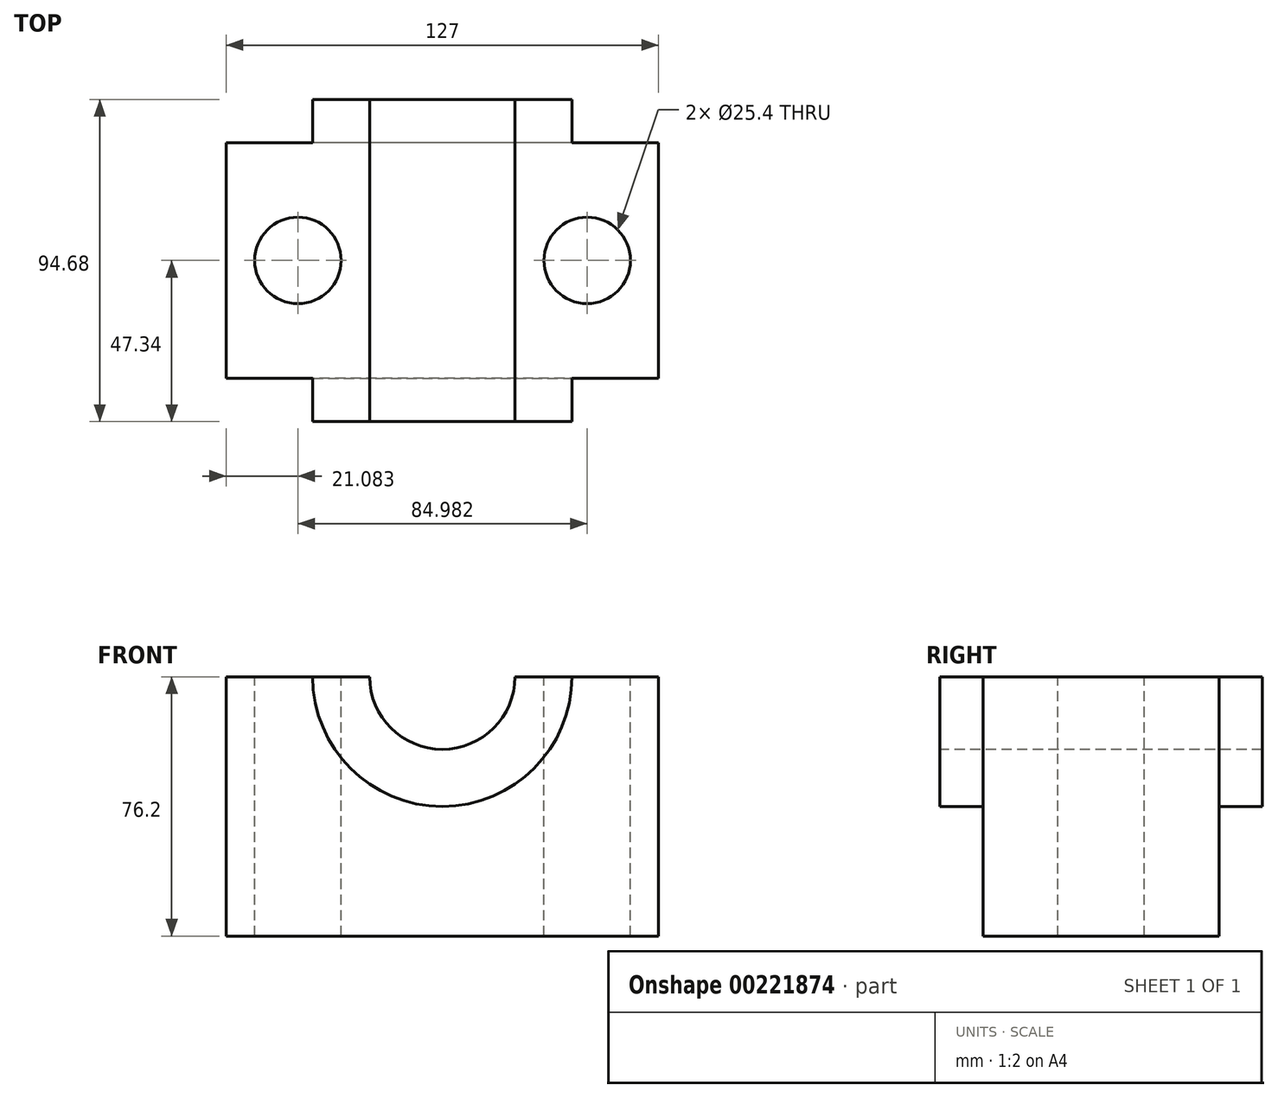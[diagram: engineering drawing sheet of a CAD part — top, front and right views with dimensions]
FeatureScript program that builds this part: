
annotation { "Feature Type Name" : "Feature", "Feature Type Description" : "" }
export const myFeature = defineFeature(function(context is Context, id is Id, definition is map)
    precondition{}
    {
        {
            var Q0;
            Q0=qCreatedBy(makeId("Top.planeOp"),FACE);
            var sketch = newSketch(context, id + "F0", { "sketchPlane" : qUnion([Q0])});
            skLineSegment(sketch, "E0.bottom", {"start": v(63.5, -34.64) * mm, "end": v(38.1, -34.64) * mm});
            skLineSegment(sketch, "E0.top", {"start": v(63.5, 34.64) * mm, "end": v(38.1, 34.64) * mm});
            skLineSegment(sketch, "E0.left", {"start": v(63.5, -34.64) * mm, "end": v(63.5, 34.64) * mm});
            skLineSegment(sketch, "E0.right", {"start": v(-63.5, -34.64) * mm, "end": v(-63.5, 34.64) * mm});
            skPoint(sketch, "E0.middle", {"position": v(0, 0) * mm});
            skLineSegment(sketch, "E1.bottom", {"start": v(-38.1, 47.34) * mm, "end": v(38.1, 47.34) * mm});
            skLineSegment(sketch, "E1.top", {"start": v(-38.1, -47.34) * mm, "end": v(38.1, -47.34) * mm});
            skLineSegment(sketch, "E1.left", {"start": v(-38.1, 47.34) * mm, "end": v(-38.1, 34.64) * mm});
            skLineSegment(sketch, "E1.right", {"start": v(38.1, 47.34) * mm, "end": v(38.1, 34.64) * mm});
            skLineSegment(sketch, "E2.trimOffspring", {"start": v(-38.1, -34.64) * mm, "end": v(-38.1, -47.34) * mm});
            skLineSegment(sketch, "E3.trimOffspring", {"start": v(-38.1, 34.64) * mm, "end": v(-63.5, 34.64) * mm});
            skLineSegment(sketch, "E4.trimOffspring", {"start": v(38.1, -34.64) * mm, "end": v(38.1, -47.34) * mm});
            skLineSegment(sketch, "E5.trimOffspring", {"start": v(-38.1, -34.64) * mm, "end": v(-63.5, -34.64) * mm});
            skSolve(sketch);
        }
        {
            var Q0;
            Q0 = qSketchRegion(id + "F0", true);
            extrude(context, id + "F1", {"entities" : qUnion([Q0]), "depth" : 76.2 * mm});
        }
        {
            var Q0;
            Q0=makeQuery(id+"F1.opExtrude","SWEPT_FACE",FACE,{"disambiguationData":[OSD([sQuery(id+"F0.wireOp",EDGE,"E1.top")])]});
            var sketch = newSketch(context, id + "F2", { "sketchPlane" : qUnion([Q0])});
            skCircle(sketch, "E6", {"center": v(0, 76.2) * mm, "radius": 38.1 * mm});
            skCircle(sketch, "E7", {"center": v(0, 76.2) * mm, "radius": 21.33 * mm});
            skLineSegment(sketch, "E8", {"start": v(-38.1, 76.2) * mm, "end": v(-38.1, 0) * mm});
            skLineSegment(sketch, "E9", {"start": v(-38.1, 0) * mm, "end": v(38.1, 0) * mm});
            skLineSegment(sketch, "E10", {"start": v(38.1, 0) * mm, "end": v(38.1, 76.2) * mm});
            skSolve(sketch);
        }
        {
            var Q0;
            {var subQ0=sQuery(id+"F2.wireOp",EDGE,"E8");Q0=makeQuery(id+"F2.imprint","IMPRINT",FACE,{"disambiguationData":[TD([[makeQuery(id+"F2.imprint","IMPRINT",EDGE,{"derivedFrom":subQ0}),1.0]])]});}
            var Q1;
            {var subQ1=makeQuery(id+"F1.opExtrude","CAP_EDGE",EDGE,{"disambiguationData":[OSD([sQuery(id+"F0.wireOp",EDGE,"E1.top")])],"isStart":false});var subQ4=sQuery(id+"F2.wireOp",EDGE,"E7");var subQ5=makeQuery(id+"F2.imprint","INTERSECT",VERTEX,{"disambiguationData":[OD(0.0)],"derivedFrom":[subQ1,subQ4]});Q1=makeQuery(id+"F2.imprint","IMPRINT",FACE,{"disambiguationData":[TD([[makeQuery(id+"F2.imprint","IMPRINT",EDGE,{"disambiguationData":[TD([[subQ5,1.0]])],"derivedFrom":subQ4}),-1.0]])]});}
            var Q2;
            {var subQ0=sQuery(id+"F2.wireOp",EDGE,"E7");var subQ1=makeQuery(id+"F1.opExtrude","CAP_EDGE",EDGE,{"disambiguationData":[OSD([sQuery(id+"F0.wireOp",EDGE,"E1.top")])],"isStart":false});var subQ2=makeQuery(id+"F2.imprint","INTERSECT",VERTEX,{"disambiguationData":[OD(0.0)],"derivedFrom":[subQ1,subQ0]});Q2=makeQuery(id+"F2.imprint","IMPRINT",FACE,{"disambiguationData":[TD([[makeQuery(id+"F2.imprint","IMPRINT",EDGE,{"disambiguationData":[TD([[subQ2,-1.0]])],"derivedFrom":subQ0}),1.0]])]});}
            extrude(context, id + "F3", {"entities" : qUnion([Q0, Q1, Q2]), "operationType" : NewBodyOperationType.REMOVE, "oppositeDirection" : true, "depth" : 12.7 * mm});
        }
        {
            var Q0;
            Q0=makeQuery(id+"F3.boolean.opBoolean","COPY",FACE,{"derivedFrom":makeQuery(id+"F3.opExtrude","CAP_FACE",FACE,{"disambiguationData":[OSD([sQuery(id+"F0.wireOp",EDGE,"E1.top"),sQuery(id+"F2.wireOp",EDGE,"E7")])],"isStart":false})});
            var sketch = newSketch(context, id + "F4", { "sketchPlane" : qUnion([Q0])});
            skCircle(sketch, "E11", {"center": v(0, 76.2) * mm, "radius": 21.33 * mm});
            skSolve(sketch);
        }
        {
            var Q0;
            Q0 = qSketchRegion(id + "F4", true);
            extrude(context, id + "F5", {"entities" : qUnion([Q0]), "operationType" : NewBodyOperationType.REMOVE, "oppositeDirection" : true, "depth" : 101.6 * mm});
        }
        {
            var Q0;
            Q0=makeQuery(id+"F1.opExtrude","SWEPT_FACE",FACE,{"disambiguationData":[OSD([sQuery(id+"F0.wireOp",EDGE,"E1.bottom")])]});
            var sketch = newSketch(context, id + "F6", { "sketchPlane" : qUnion([Q0])});
            skArc(sketch, "E12", {"start": v(-38.1, 76.2) * mm, "mid": v(0, 38.1) * mm, "end": v(38.1, 76.2) * mm});
            skLineSegment(sketch, "E13", {"start": v(-38.1, 76.2) * mm, "end": v(-38.1, 0) * mm});
            skLineSegment(sketch, "E14", {"start": v(-38.1, 0) * mm, "end": v(38.1, 0) * mm});
            skLineSegment(sketch, "E15", {"start": v(38.1, 0) * mm, "end": v(38.1, 76.2) * mm});
            skSolve(sketch);
        }
        {
            var Q0;
            Q0 = qSketchRegion(id + "F6", true);
            extrude(context, id + "F7", {"entities" : qUnion([Q0]), "operationType" : NewBodyOperationType.REMOVE, "oppositeDirection" : true, "depth" : 12.7 * mm});
        }
        {
            var Q0;
            {var subQ1=sQuery(id+"F0.wireOp",EDGE,"E1.top");var subQ6=sQuery(id+"F0.wireOp",EDGE,"E5.trimOffspring");var subQ7=sQuery(id+"F0.wireOp",EDGE,"E3.trimOffspring");var subQ8=sQuery(id+"F0.wireOp",EDGE,"E1.left");var subQ9=sQuery(id+"F0.wireOp",EDGE,"E0.bottom");var subQ10=sQuery(id+"F0.wireOp",EDGE,"E0.right");var subQ11=sQuery(id+"F0.wireOp",EDGE,"E1.bottom");Q0=makeQuery(id+"F5.boolean.opBoolean","SPLIT",FACE,{"disambiguationData":[TD([makeQuery(id+"F1.opExtrude","SWEPT_FACE",FACE,{"disambiguationData":[OSD([subQ10])]})])],"derivedFrom":makeQuery(id+"F1.opExtrude","CAP_FACE",FACE,{"disambiguationData":[OSD([subQ9,sQuery(id+"F0.wireOp",EDGE,"E0.top"),sQuery(id+"F0.wireOp",EDGE,"E0.left"),subQ10,subQ11,subQ1,subQ8,sQuery(id+"F0.wireOp",EDGE,"E1.right"),sQuery(id+"F0.wireOp",EDGE,"E2.trimOffspring"),subQ7,sQuery(id+"F0.wireOp",EDGE,"E4.trimOffspring"),subQ6])],"isStart":false})});}
            var sketch = newSketch(context, id + "F8", { "sketchPlane" : qUnion([Q0])});
            skLineSegment(sketch, "E16", {"start": v(-21.33, 0) * mm, "end": v(-63.5, 0) * mm});
            skLineSegment(sketch, "E17", {"start": v(21.65, 0) * mm, "end": v(63.48, 0) * mm});
            skCircle(sketch, "E18", {"center": v(-42.42, 0) * mm, "radius": 12.7 * mm});
            skCircle(sketch, "E19", {"center": v(42.56, 0) * mm, "radius": 12.7 * mm});
            skSolve(sketch);
        }
        {
            var Q0;
            {var subQ0=sQuery(id+"F8.wireOp",EDGE,"E19");var subQ1=sQuery(id+"F8.wireOp",EDGE,"E17");var subQ2=makeQuery(id+"F8.imprint","INTERSECT",VERTEX,{"disambiguationData":[OD(0.0)],"derivedFrom":[subQ1,subQ0]});Q0=makeQuery(id+"F8.imprint","IMPRINT",FACE,{"disambiguationData":[TD([[makeQuery(id+"F8.imprint","IMPRINT",EDGE,{"disambiguationData":[TD([[subQ2,-1.0]])],"derivedFrom":subQ1}),-1.0]])]});}
            var Q1;
            {var subQ0=sQuery(id+"F8.wireOp",EDGE,"E19");var subQ1=sQuery(id+"F8.wireOp",EDGE,"E17");var subQ2=makeQuery(id+"F8.imprint","INTERSECT",VERTEX,{"disambiguationData":[OD(0.0)],"derivedFrom":[subQ1,subQ0]});Q1=makeQuery(id+"F8.imprint","IMPRINT",FACE,{"disambiguationData":[TD([[makeQuery(id+"F8.imprint","IMPRINT",EDGE,{"disambiguationData":[TD([[subQ2,-1.0]])],"derivedFrom":subQ1}),1.0]])]});}
            var Q2;
            {var subQ0=sQuery(id+"F8.wireOp",EDGE,"E18");var subQ1=sQuery(id+"F8.wireOp",EDGE,"E16");var subQ2=makeQuery(id+"F8.imprint","INTERSECT",VERTEX,{"disambiguationData":[OD(0.0)],"derivedFrom":[subQ1,subQ0]});Q2=makeQuery(id+"F8.imprint","IMPRINT",FACE,{"disambiguationData":[TD([[makeQuery(id+"F8.imprint","IMPRINT",EDGE,{"disambiguationData":[TD([[subQ2,-1.0]])],"derivedFrom":subQ1}),1.0]])]});}
            var Q3;
            {var subQ0=sQuery(id+"F8.wireOp",EDGE,"E18");var subQ1=sQuery(id+"F8.wireOp",EDGE,"E16");var subQ2=makeQuery(id+"F8.imprint","INTERSECT",VERTEX,{"disambiguationData":[OD(0.0)],"derivedFrom":[subQ1,subQ0]});Q3=makeQuery(id+"F8.imprint","IMPRINT",FACE,{"disambiguationData":[TD([[makeQuery(id+"F8.imprint","IMPRINT",EDGE,{"disambiguationData":[TD([[subQ2,-1.0]])],"derivedFrom":subQ1}),-1.0]])]});}
            extrude(context, id + "F9", {"entities" : qUnion([Q0, Q1, Q2, Q3]), "operationType" : NewBodyOperationType.REMOVE, "oppositeDirection" : true, "depth" : 127 * mm});
        }
    });
